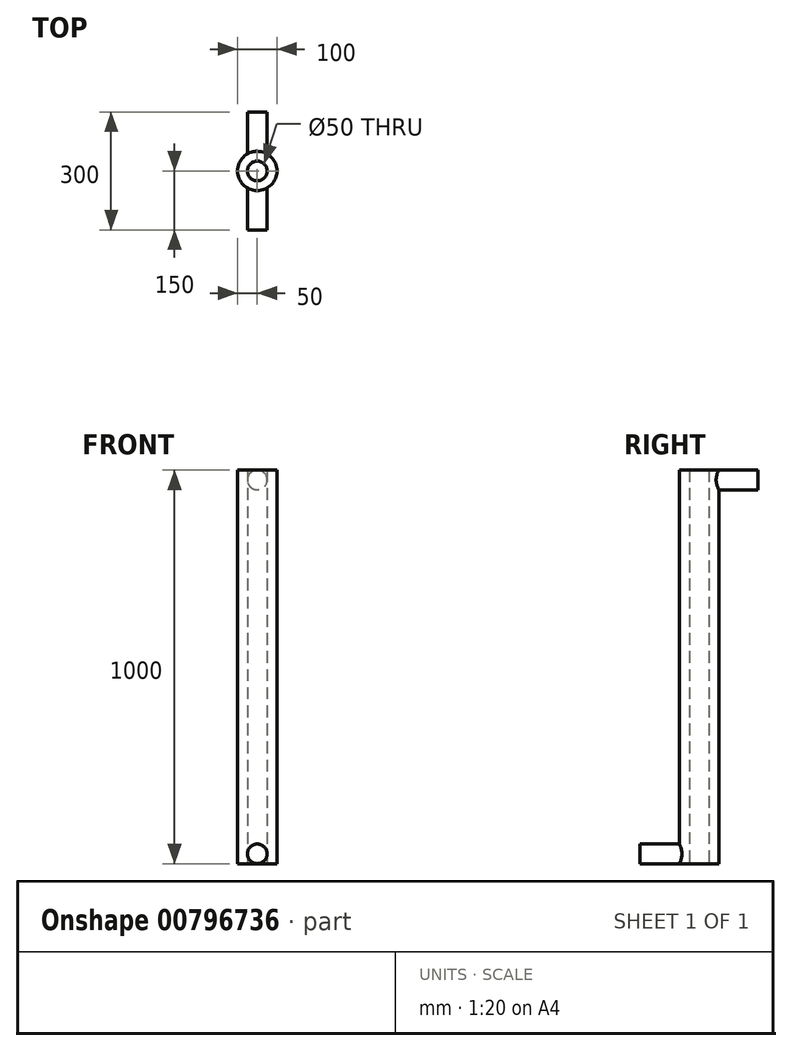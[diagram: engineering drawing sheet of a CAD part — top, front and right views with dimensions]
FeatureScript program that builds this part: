
annotation { "Feature Type Name" : "Feature", "Feature Type Description" : "" }
export const myFeature = defineFeature(function(context is Context, id is Id, definition is map)
    precondition{}
    {
        {
            var Q0;
            Q0=qCreatedBy(makeId("Top.planeOp"),FACE);
            var sketch = newSketch(context, id + "F0", { "sketchPlane" : qUnion([Q0])});
            skCircle(sketch, "E0", {"center": v(0, 0) * mm, "radius": 25 * mm});
            skCircle(sketch, "E1", {"center": v(0, 0) * mm, "radius": 50 * mm});
            skSolve(sketch);
        }
        {
            var Q0;
            Q0=makeQuery(id+"F0.imprint","IMPRINT",FACE,{"disambiguationData":[TD([[makeQuery(id+"F0.imprint","IMPRINT",EDGE,{"derivedFrom":sQuery(id+"F0.wireOp",EDGE,"E0")}),-1.0]])]});
            extrude(context, id + "F1", {"entities" : qUnion([Q0]), "depth" : 1000 * mm, "offsetDistance" : 25 * mm});
        }
        {
            var Q0;
            Q0=qCreatedBy(makeId("Front.planeOp"),FACE);
            cPlane(context, id + "F2", {"entities" : qUnion([Q0]), "cplaneType" : CPlaneType.OFFSET, "offset" : 50 * mm, "width" : 150 * mm, "height" : 150 * mm});
        }
        {
            var Q0;
            Q0=qCreatedBy(id+"F2.planeOp",FACE);
            var sketch = newSketch(context, id + "F3", { "sketchPlane" : qUnion([Q0])});
            skCircle(sketch, "E2", {"center": v(0, 25) * mm, "radius": 25 * mm});
            skSolve(sketch);
        }
        {
            var Q0;
            Q0=qCreatedBy(makeId("Front.planeOp"),FACE);
            cPlane(context, id + "F4", {"entities" : qUnion([Q0]), "cplaneType" : CPlaneType.OFFSET, "offset" : 50 * mm, "oppositeDirection" : true, "width" : 150 * mm, "height" : 150 * mm});
        }
        {
            var Q0;
            Q0=qCreatedBy(id+"F4.planeOp",FACE);
            var sketch = newSketch(context, id + "F5", { "sketchPlane" : qUnion([Q0])});
            skCircle(sketch, "E3", {"center": v(0, 975) * mm, "radius": 25 * mm});
            skSolve(sketch);
        }
        {
            var Q0;
            Q0 = qSketchRegion(id + "F5", true);
            var Q1;
            Q1=sQuery(id+"F5.wireOp",EDGE,"E3");
            extrude(context, id + "F6", {"entities" : qUnion([Q0]), "operationType" : NewBodyOperationType.ADD, "surfaceEntities" : qUnion([Q1]), "oppositeDirection" : true, "depth" : 100 * mm, "offsetDistance" : 25 * mm, "hasSecondDirection" : true, "secondDirectionOppositeDirection" : false, "secondDirectionDepth" : 7 * mm});
        }
        {
            var Q0;
            Q0 = qSketchRegion(id + "F3", true);
            extrude(context, id + "F7", {"entities" : qUnion([Q0]), "operationType" : NewBodyOperationType.ADD, "depth" : 100 * mm, "offsetDistance" : 25 * mm, "hasSecondDirection" : true, "secondDirectionOppositeDirection" : true, "secondDirectionDepth" : 7 * mm});
        }
    });
